# Revit family: PRD_AR_WstBns_RODANWasteBin_RODX606_RODX606E
name_source: partatom
category: Specialty Equipment
revit_build: Autodesk Revit 2018 (Build: 20190510_1515(x64)
units: mm (PartAtom-declared; Revit-internal decimal feet)

## family parameters
Cut with Voids When Loaded = Yes
Host = Face
OmniClass Number = 23.40.20.31.11
OmniClass Title = Bins
Part Type = Normal
Room Calculation Point = No
Round Connector Dimension = Use Diameter
Shared = No

## types (2) — shared parameters
AssetType = Fixed
BagHolder = Integrated
Category = Pr_40_50_07_96, Waste bins
Default Elevation = 800 mm  [stored 2.62467 ft]
DurationUnit = year
Features = stainless steel, surface satin finished
FillingVolume = 45.00 liter
Finish = satin finished
IfcExportAs = IfcFurnitureType
IfcExportType = USERDEFINED
IntegralAccessories = incl. stainless steel screws and dowels
IsBuiltIn = TRUE
Lid = Yes
Lock = Key-lock
MainColor = stainless steel
Manufacturer = KWC Group AG
ManufacturerName = KWC Group AG
ManufacturerURL = www.kwc.com
Material = stainless steel
MaterialCode = 1.4301
MaterialThickness = 0.80 mm
NBSDescription = Waste bins
NBSReference = 45-35-72/380
NominalDepth = 153 mm  [stored 0.501969 ft]
ProductInformation = https://pim.kwc.com
Style = waste bin
TypeOfFixing = Screw
URL = www.kwc.com
Uniclass2015Code = Pr_40_50_07_96
Uniclass2015Title = Waste bins
Uniclass2015Version = Products v1.10
Version = 1
WarrantyDurationUnit = year
WasteBinMaterial = PRD_AR_StainlessSteel_SatinFinished

## per-type parameters (varying)
| type | BIMObjectName | Description | GrossWeight | ModelNumber | ModelOffset | Name | NetWeight | NominalHeight | NominalWidth | Size | TypeOfMounting | VoidOffset |
| RODX606 | PRD_AR_WasteBins_RODANWasteBin_RODX606 | Waste bin for wall mounting, stainless steel, surface satin finished, material thickness 0.8 mm, folding self closing lid, with integrated bag holder, cylinder lock with KWC standard key, inclusive stainless steel screws and dowels. Capacity approx. 45 liters. | 9.15 kg | 2000101346 | 142 mm  [stored 0.465879 ft] | Waste Bin RODX606 | 7.62 kg | 710 mm  [stored 2.3294 ft] | 495 mm  [stored 1.62402 ft] | 495 x 710 x 153 mm | Wall mounting | 110 mm  [stored 0.360892 ft] |
| RODX606E | PRD_AR_WasteBins_RODANWasteBin_RODX606E | Waste bin for recessed mounting, stainless steel, surface satin finished, material thickness 0.8 mm, folding self closing lid, with integrated bag holder, cylinder lock with KWC standard key, inclusive stainless steel screws and dowels. Capacity approx. 45 liters. | 10.01 kg | 2000101348 | 0 mm  [stored 0 ft] | Waste Bin RODX606E | 8.34 kg | 750 mm  [stored 2.46063 ft] | 535 mm  [stored 1.75525 ft] | 535 x 750 x 153 mm | Recessed mounting | 133 mm  [stored 0.436352 ft] |

note: column(s) folded — value = type name in every type: Model, ModelReference, Type

note: [stored X ft] marks values corroborated as IEEE doubles in the binary element streams (Revit-internal decimal feet)

## geometry (parser evidence)
native form markers: Sweep x1
no freeform markers — native parametric forms only
